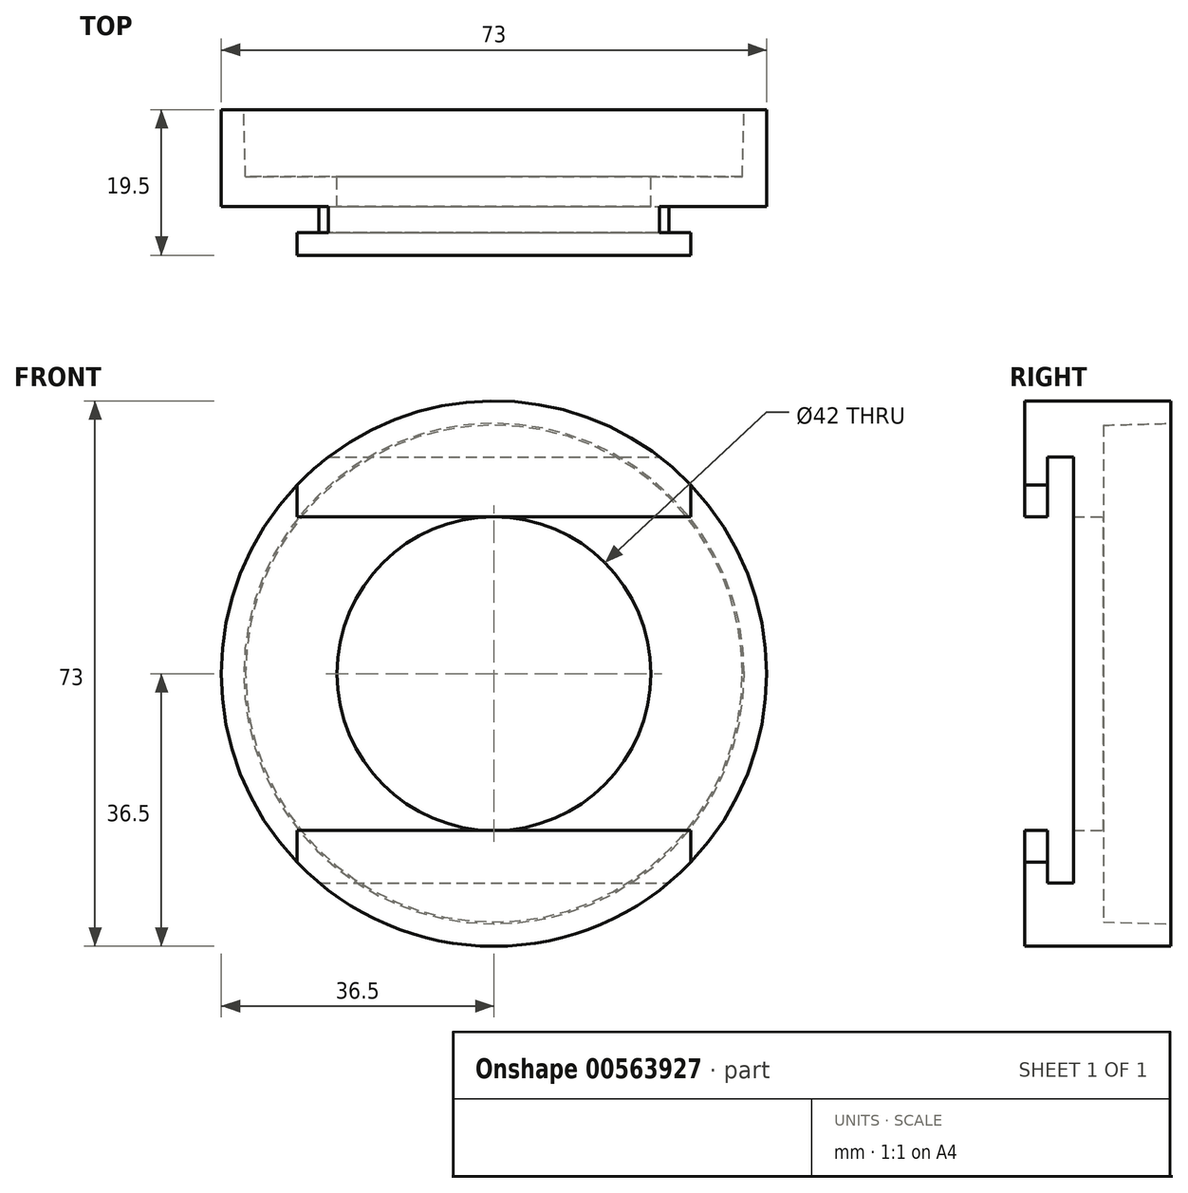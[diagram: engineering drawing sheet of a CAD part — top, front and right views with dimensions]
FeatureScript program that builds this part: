
annotation { "Feature Type Name" : "Feature", "Feature Type Description" : "" }
export const myFeature = defineFeature(function(context is Context, id is Id, definition is map)
    precondition{}
    {
        {
            var Q0;
            Q0=qCreatedBy(makeId("Front.planeOp"),FACE);
            var sketch = newSketch(context, id + "F0", { "sketchPlane" : qUnion([Q0])});
            skCircle(sketch, "E0", {"center": v(0, 0) * mm, "radius": 36.5 * mm});
            skSolve(sketch);
        }
        {
            var Q0;
            Q0 = qSketchRegion(id + "F0", true);
            extrude(context, id + "F1", {"entities" : qUnion([Q0]), "depth" : 19.5 * mm, "offsetDistance" : 25 * mm});
        }
        {
            var Q0;
            Q0=qCreatedBy(makeId("Front.planeOp"),FACE);
            cPlane(context, id + "F2", {"entities" : qUnion([Q0]), "cplaneType" : CPlaneType.OFFSET, "offset" : 9 * mm, "width" : 150 * mm, "height" : 150 * mm});
        }
        {
            var Q0;
            Q0=qCreatedBy(id+"F2.planeOp",FACE);
            var sketch = newSketch(context, id + "F3", { "sketchPlane" : qUnion([Q0])});
            skCircle(sketch, "E1", {"center": v(0, 0) * mm, "radius": 21 * mm});
            skSolve(sketch);
        }
        {
            var Q0;
            Q0 = qSketchRegion(id + "F3", true);
            extrude(context, id + "F4", {"entities" : qUnion([Q0]), "operationType" : NewBodyOperationType.REMOVE, "depth" : 4 * mm, "offsetDistance" : 25 * mm});
        }
        {
            var Q0;
            Q0=qCreatedBy(makeId("Top.planeOp"),FACE);
            cPlane(context, id + "F5", {"entities" : qUnion([Q0]), "cplaneType" : CPlaneType.OFFSET, "offset" : 21 * mm, "width" : 150 * mm, "height" : 150 * mm});
        }
        {
            var Q0;
            Q0=qCreatedBy(makeId("Front.planeOp"),FACE);
            cPlane(context, id + "F6", {"entities" : qUnion([Q0]), "cplaneType" : CPlaneType.OFFSET, "offset" : 19.5 * mm, "width" : 150 * mm, "height" : 150 * mm});
        }
        {
            var Q0;
            Q0=qCreatedBy(id+"F6.planeOp",FACE);
            var sketch = newSketch(context, id + "F7", { "sketchPlane" : qUnion([Q0])});
            skLineSegment(sketch, "E2.bottom", {"start": v(-37.22, 21) * mm, "end": v(37.76, 21) * mm});
            skLineSegment(sketch, "E2.top", {"start": v(-37.22, -21) * mm, "end": v(37.76, -21) * mm});
            skLineSegment(sketch, "E2.left", {"start": v(-37.22, 21) * mm, "end": v(-37.22, -21) * mm});
            skLineSegment(sketch, "E2.right", {"start": v(37.76, 21) * mm, "end": v(37.76, -21) * mm});
            skSolve(sketch);
        }
        {
            var Q0;
            Q0 = qSketchRegion(id + "F7", true);
            extrude(context, id + "F8", {"entities" : qUnion([Q0]), "operationType" : NewBodyOperationType.REMOVE, "oppositeDirection" : true, "depth" : 6.5 * mm, "offsetDistance" : 25 * mm});
        }
        {
            var Q0;
            Q0=qCreatedBy(makeId("Right.planeOp"),FACE);
            var sketch = newSketch(context, id + "F9", { "sketchPlane" : qUnion([Q0])});
            skLineSegment(sketch, "E3.bottom", {"start": v(-13, 29) * mm, "end": v(-16.5, 29) * mm});
            skLineSegment(sketch, "E3.top", {"start": v(-13, -28) * mm, "end": v(-16.5, -28) * mm});
            skLineSegment(sketch, "E3.left", {"start": v(-13, 29) * mm, "end": v(-13, -28) * mm});
            skLineSegment(sketch, "E3.right", {"start": v(-16.5, 29) * mm, "end": v(-16.5, -28) * mm});
            skSolve(sketch);
        }
        {
            var Q0;
            Q0 = qSketchRegion(id + "F9", true);
            extrude(context, id + "F10", {"entities" : qUnion([Q0]), "operationType" : NewBodyOperationType.REMOVE, "endBound" : BoundingType.SYMMETRIC, "oppositeDirection" : true, "depth" : 60 * mm, "offsetDistance" : 25 * mm});
        }
        {
            var Q0;
            Q0=makeQuery(id+"F8.boolean.opBoolean","INTERSECT",EDGE,{"disambiguationData":[OD(0.0)],"derivedFrom":[makeQuery(id+"F1.opExtrude","SWEPT_FACE",FACE,{"disambiguationData":[OSD([sQuery(id+"F0.wireOp",EDGE,"E0")])]}),makeQuery(id+"F8.opExtrude","SWEPT_FACE",FACE,{"disambiguationData":[OSD([sQuery(id+"F7.wireOp",EDGE,"E2.bottom")])]})]});
            chamfer(context, id + "F11", {"entities" : qUnion([Q0]), "chamferType" : ChamferType.OFFSET_ANGLE, "width" : 3 * mm, "oppositeDirection" : false, "angle" : 90 * degree, "tangentPropagation" : true});
        }
        {
            var Q0;
            Q0=makeQuery(id+"F8.boolean.opBoolean","INTERSECT",EDGE,{"disambiguationData":[OD(1.0)],"derivedFrom":[makeQuery(id+"F1.opExtrude","SWEPT_FACE",FACE,{"disambiguationData":[OSD([sQuery(id+"F0.wireOp",EDGE,"E0")])]}),makeQuery(id+"F8.opExtrude","SWEPT_FACE",FACE,{"disambiguationData":[OSD([sQuery(id+"F7.wireOp",EDGE,"E2.bottom")])]})]});
            chamfer(context, id + "F12", {"entities" : qUnion([Q0]), "chamferType" : ChamferType.OFFSET_ANGLE, "width" : 3 * mm, "oppositeDirection" : false, "angle" : 90 * degree, "tangentPropagation" : true});
        }
        {
            var Q0;
            Q0=makeQuery(id+"F8.boolean.opBoolean","INTERSECT",EDGE,{"disambiguationData":[OD(0.0)],"derivedFrom":[makeQuery(id+"F1.opExtrude","SWEPT_FACE",FACE,{"disambiguationData":[OSD([sQuery(id+"F0.wireOp",EDGE,"E0")])]}),makeQuery(id+"F8.opExtrude","SWEPT_FACE",FACE,{"disambiguationData":[OSD([sQuery(id+"F7.wireOp",EDGE,"E2.top")])]})]});
            chamfer(context, id + "F13", {"entities" : qUnion([Q0]), "chamferType" : ChamferType.OFFSET_ANGLE, "width" : 3 * mm, "oppositeDirection" : true, "angle" : 90 * degree, "tangentPropagation" : true});
        }
        {
            var Q0;
            Q0=makeQuery(id+"F8.boolean.opBoolean","INTERSECT",EDGE,{"disambiguationData":[OD(1.0)],"derivedFrom":[makeQuery(id+"F1.opExtrude","SWEPT_FACE",FACE,{"disambiguationData":[OSD([sQuery(id+"F0.wireOp",EDGE,"E0")])]}),makeQuery(id+"F8.opExtrude","SWEPT_FACE",FACE,{"disambiguationData":[OSD([sQuery(id+"F7.wireOp",EDGE,"E2.top")])]})]});
            chamfer(context, id + "F14", {"entities" : qUnion([Q0]), "chamferType" : ChamferType.OFFSET_ANGLE, "width" : 3 * mm, "oppositeDirection" : true, "angle" : 90 * degree, "tangentPropagation" : true});
        }
        {
            var Q0;
            Q0=qCreatedBy(makeId("Right.planeOp"),FACE);
            var sketch = newSketch(context, id + "F15", { "sketchPlane" : qUnion([Q0])});
            skLineSegment(sketch, "E4", {"start": v(0, 0) * mm, "end": v(0, 33.5) * mm});
            skLineSegment(sketch, "E5", {"start": v(0, 33.5) * mm, "end": v(-9, 33.25) * mm});
            skLineSegment(sketch, "E6", {"start": v(-9, 33.25) * mm, "end": v(-9, 0) * mm});
            skLineSegment(sketch, "E7", {"start": v(-9, 0) * mm, "end": v(0, 0) * mm});
            skSolve(sketch);
        }
        {
            var Q0;
            Q0 = qSketchRegion(id + "F15", true);
            var Q1;
            Q1=sQuery(id+"F15.wireOp",EDGE,"E7");
            revolve(context, id + "F16", {"operationType" : NewBodyOperationType.REMOVE, "entities" : qUnion([Q0]), "axis" : qUnion([Q1]), "revolveType" : RevolveType.FULL, "oppositeDirection" : true});
        }
    });
